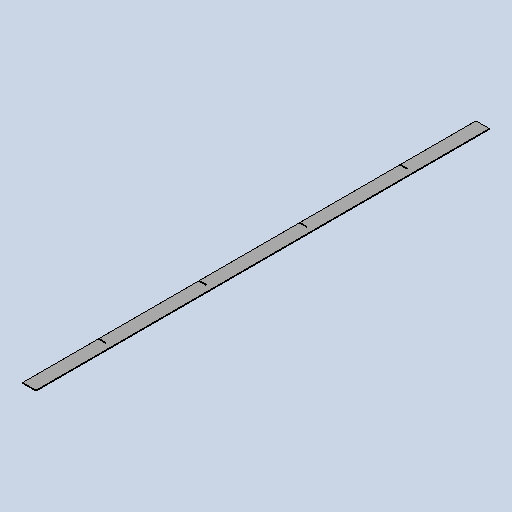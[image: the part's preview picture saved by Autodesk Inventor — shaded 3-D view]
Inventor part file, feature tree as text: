
AUTODESK INVENTOR PART (.ipt)
format: ipt  version: 2025 (Build 290162010, 162A)  size: 147,968 bytes
history: native  units: mm
features: other x3, sketch x2, sheet_metal_op x1, extrude x1
ambient origin geometry x8: Origin, YZ Plane, XZ Plane, XY Plane, X Axis, Y Axis, Z Axis, Center Point
bodies: Solid1 (feature_tree)
feature tree (7):
  other  "MSC 0163 rib cone exit back"
  sheet_metal_op  "Face1"
  extrude  "Extrusion1"  Depth=1700.0mm
  sketch  "Sketch1"  dims[d0=50.0mm d1=1700.0mm]
  other  "Plate1"
  sketch  "Sketch2"  dims[d2=3.0mm d15=26.0mm d16=3.0mm d17=188.5mm d18=0.0mm d19=0.0mm d20=26.0mm d21=3.0mm d22=377.0mm d23=26.0mm d24=3.0mm d25=188.5mm d26=377.0mm d27=3.0mm d28=26.0mm]
  other  "Definition1"
